# Revit family: VLN_VenlomixMedical_A5548_BIM_NL
name_source: partatom
category: Plumbing Fixtures
revit_build: Autodesk Revit MEP 2014 (Build: 20130308_1515(x64)
units: mm (PartAtom-declared; Revit-internal decimal feet)

## types (1)
- A5548AA - VMIX-MED SNK THERM MXR R-MTD T.SPT & LVR
    Accessories = www.idealspec.co.uk
    AreaUnits = millimeters
    Assembly Code = C1030200
    AssetType = Fixed
    BIMObjectName = Venlo_WaterSupplyFittingsForSinks_VenlomixMedical_A5548AA
    BREEAMApproved = No
    BarCode = 4015413326025
    Brand = Venlo
    CWFU = 0
    Color = Chrome
    ConnectionType = Plumbing
    Cost = 0 $
    Default Elevation = 800 mm  [stored 2.62467 ft]
    Description = Vmix-Med Sink Thermostatic Mixer Tubular Spout & Lever
    DurationUnit = year
    ECA = No
    ExpectedLife = 30
    FaucetFunction = MIXED
    FaucetOperation = LEVERHANDLE
    FaucetType = PILLAR
    Features = Sink Thermostatic Mixer Tubular Spout & Lever
    Finish = Chrome
    HWFU = 0
    Help = www.idealspec.co.uk/contact-us.html
    IfcExportAs = IfcValveType
    IfcExportType = FAUCET
    InstallationInstructions = www.idealspec.co.uk/resources.html
    LinearUnits = millimeters
    ManufacturerURL = www.idealspec.co.uk
    Material = Brass
    Model = A5548AA
    ModelNumber = A5548AA
    NBSDescription = Water supply fittings for sinks
    NBSReference = 45-35-70/345
    Name = WaterSupplyFittingsForSinks_VenlomixMedical_A5548AA_Venlo
    NettWeight = 2.856
    NominalHeight = 331 mm
    NominalLength = 242 mm
    NominalWidth = 275 mm
    ProductInformation = www.idealspec.co.uk/assets/datasheet/A5548AA
    Shape = Sculptured
    Size = 275 x 242 x 331 mm
    Space = Internal
    SpareParts = www.fastpart-spares.co.uk
    TMV3 = Yes
    TestPressure = 10 Bar
    URL = www.idealspec.co.uk
    Uniclass2015Code = Pr_40_20_87_84
    Uniclass2015Title = Sink taps
    Uniclass2015Version = Products v1.1
    ValveMechanism = ceramic disc
    ValveOperation = lever
    Version = 1
    VolumeUnits = Litres
    WFU = 0
    WRAS = Yes
    WarrantyDescription = Manufacturers Warranty
    WarrantyDurationParts = 5
    WarrantyDurationUnit = year
    WaterEfficientProduct = No
    WorkingPressure = 0.5-3 Bar

note: [stored X ft] marks values corroborated as IEEE doubles in the binary element streams (Revit-internal decimal feet)

## geometry (parser evidence)
native form markers: Sweep x2
no freeform markers — native parametric forms only
